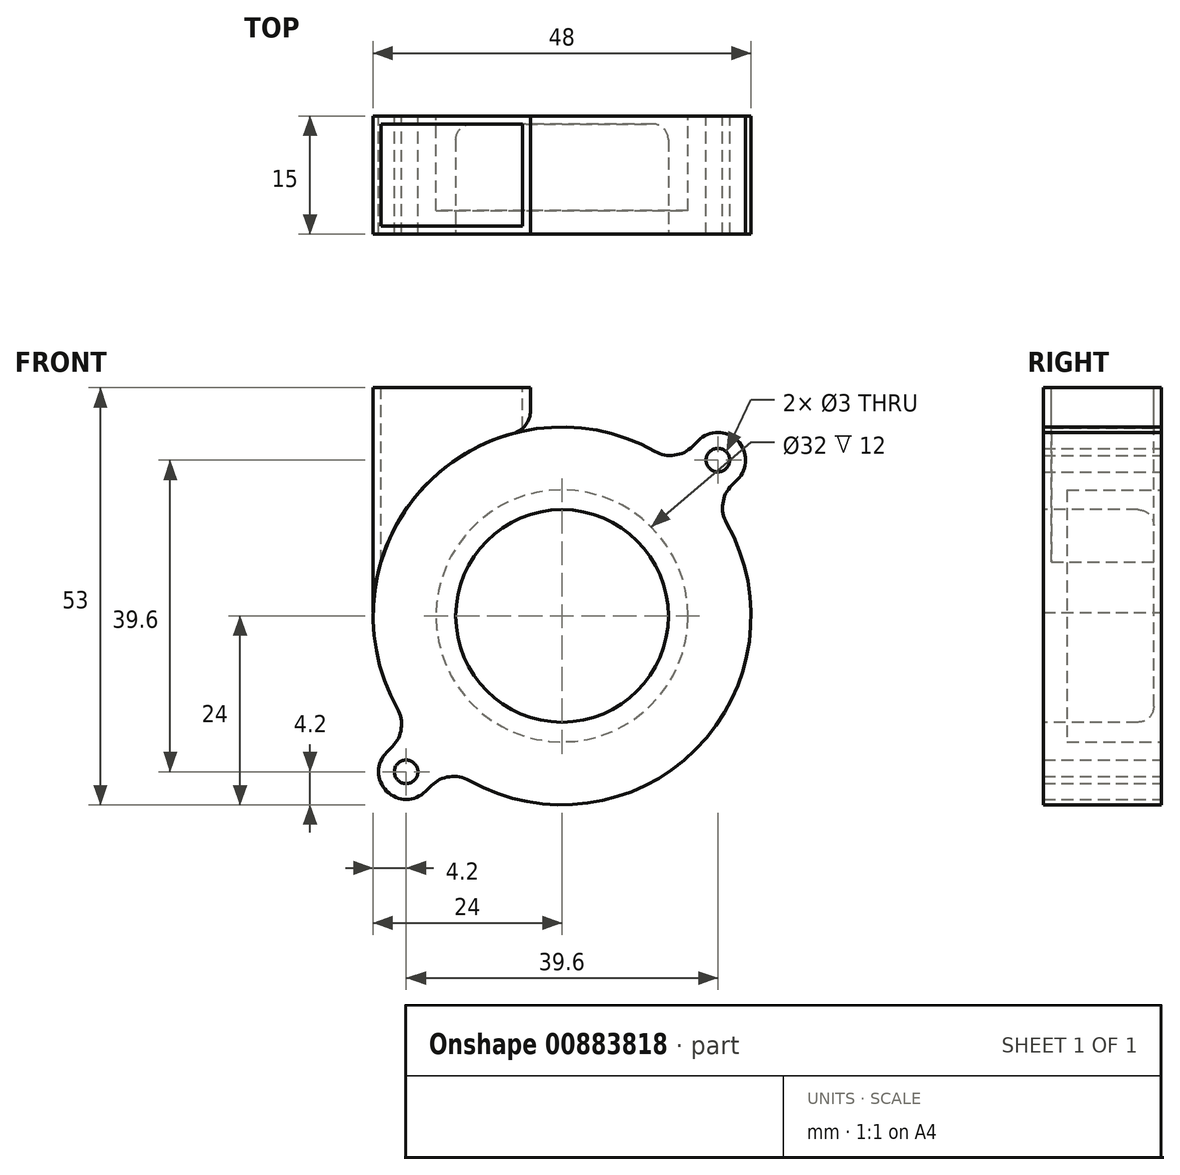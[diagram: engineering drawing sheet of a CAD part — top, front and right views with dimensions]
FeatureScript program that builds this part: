
annotation { "Feature Type Name" : "Feature", "Feature Type Description" : "" }
export const myFeature = defineFeature(function(context is Context, id is Id, definition is map)
    precondition{}
    {
        {
            var Q0;
            Q0=qCreatedBy(makeId("Front.planeOp"),FACE);
            var sketch = newSketch(context, id + "F0", { "sketchPlane" : qUnion([Q0])});
            skArc(sketch, "E0", {"start": v(-11.8, -20.9) * mm, "mid": v(16.97, -16.97) * mm, "end": v(20.9, 11.8) * mm});
            skLineSegment(sketch, "E1", {"start": v(-38.26, -38.26) * mm, "end": v(35.98, 35.98) * mm, "construction": true});
            skCircle(sketch, "E2", {"center": v(-19.8, -19.8) * mm, "radius": 1.5 * mm});
            skCircle(sketch, "E3", {"center": v(19.8, 19.8) * mm, "radius": 1.5 * mm});
            skArc(sketch, "E4", {"start": v(-22.27, -17.32) * mm, "mid": v(-22.27, -22.27) * mm, "end": v(-17.32, -22.27) * mm});
            skArc(sketch, "E5", {"start": v(22.27, 17.32) * mm, "mid": v(22.27, 22.27) * mm, "end": v(17.32, 22.27) * mm});
            skLineSegment(sketch, "E6", {"start": v(-17.32, -22.27) * mm, "end": v(-16.6, -21.55) * mm});
            skLineSegment(sketch, "E7", {"start": v(-22.27, -17.32) * mm, "end": v(-21.55, -16.6) * mm});
            skLineSegment(sketch, "E8.trimOffspring", {"start": v(16.6, 21.55) * mm, "end": v(17.32, 22.27) * mm});
            skLineSegment(sketch, "E9.trimOffspring", {"start": v(21.55, 16.6) * mm, "end": v(22.27, 17.32) * mm});
            skArc(sketch, "E10.trimOffspring", {"start": v(11.8, 20.9) * mm, "mid": v(-16.97, 16.97) * mm, "end": v(-20.9, -11.8) * mm});
            skPoint(sketch, "E11.visualSharp", {"position": v(-14.31, -19.26) * mm});
            skArc(sketch, "E11.filletArc", {"start": v(-11.8, -20.9) * mm, "mid": v(-14.31, -20.42) * mm, "end": v(-16.6, -21.55) * mm});
            skPoint(sketch, "E12.visualSharp", {"position": v(-19.26, -14.31) * mm});
            skArc(sketch, "E12.filletArc", {"start": v(-21.55, -16.6) * mm, "mid": v(-20.42, -14.31) * mm, "end": v(-20.9, -11.8) * mm});
            skPoint(sketch, "E13.visualSharp", {"position": v(19.26, 14.31) * mm});
            skArc(sketch, "E13.filletArc", {"start": v(21.55, 16.6) * mm, "mid": v(20.42, 14.31) * mm, "end": v(20.9, 11.8) * mm});
            skPoint(sketch, "E14.visualSharp", {"position": v(14.31, 19.26) * mm});
            skArc(sketch, "E14.filletArc", {"start": v(11.8, 20.9) * mm, "mid": v(14.31, 20.42) * mm, "end": v(16.6, 21.55) * mm});
            skSolve(sketch);
        }
        {
            var Q0;
            Q0=qSketchRegion(id+"F0",true);
            extrude(context, id + "F1", {"entities" : qUnion([Q0]), "depth" : 15 * mm, "offsetDistance" : 25 * mm, "symmetric" : true});
        }
        {
            var Q0;
            Q0=qCreatedBy(makeId("Top.planeOp"),FACE);
            cPlane(context, id + "F2", {"entities" : qUnion([Q0]), "cplaneType" : CPlaneType.OFFSET, "offset" : 29 * mm, "width" : 150 * mm, "height" : 150 * mm});
        }
        {
            var Q0;
            Q0=qCreatedBy(id+"F2.planeOp",FACE);
            var sketch = newSketch(context, id + "F3", { "sketchPlane" : qUnion([Q0])});
            skLineSegment(sketch, "E15.bottom", {"start": v(-4, 7.5) * mm, "end": v(-24, 7.5) * mm});
            skLineSegment(sketch, "E15.top", {"start": v(-4, -7.5) * mm, "end": v(-24, -7.5) * mm});
            skLineSegment(sketch, "E15.left", {"start": v(-4, 7.5) * mm, "end": v(-4, -7.5) * mm});
            skLineSegment(sketch, "E15.right", {"start": v(-24, 7.5) * mm, "end": v(-24, -7.5) * mm});
            skPoint(sketch, "E15.middle", {"position": v(-14, 0) * mm});
            skSolve(sketch);
        }
        {
            var Q0;
            Q0=qSketchRegion(id+"F3",true);
            var Q1;
            Q1=makeQuery(id+"F1.opExtrude","SWEPT_FACE",FACE,{"disambiguationData":[OSD([sQuery(id+"F0.wireOp",EDGE,"E0")])]});
            extrude(context, id + "F4", {"entities" : qUnion([Q0]), "operationType" : NewBodyOperationType.ADD, "endBound" : BoundingType.UP_TO_SURFACE, "oppositeDirection" : true, "depth" : 25 * mm, "endBoundEntityFace" : qUnion([Q1]), "offsetDistance" : 25 * mm});
        }
        {
            var Q0;
            Q0=makeQuery(id+"F1.opExtrude","CAP_FACE",FACE,{"disambiguationData":[OSD([sQuery(id+"F0.wireOp",EDGE,"E0")])],"isStart":true});
            var sketch = newSketch(context, id + "F5", { "sketchPlane" : qUnion([Q0])});
            skCircle(sketch, "E16", {"center": v(0, 0) * mm, "radius": 16 * mm});
            skSolve(sketch);
        }
        {
            var Q0;
            Q0=qSketchRegion(id+"F5",true);
            extrude(context, id + "F6", {"entities" : qUnion([Q0]), "operationType" : NewBodyOperationType.REMOVE, "oppositeDirection" : true, "depth" : 12 * mm, "offsetDistance" : 25 * mm});
        }
        {
            var Q0;
            Q0=makeQuery(id+"F3.imprint","IMPRINT",FACE,{"disambiguationData":[TD([[makeQuery(id+"F3.imprint","IMPRINT",EDGE,{"derivedFrom":sQuery(id+"F3.wireOp",EDGE,"E15.bottom")}),1.0]])]});
            var sketch = newSketch(context, id + "F7", { "sketchPlane" : qUnion([Q0])});
            skLineSegment(sketch, "E17.0", {"start": v(-23, -6.5) * mm, "end": v(-5, -6.5) * mm});
            skLineSegment(sketch, "E17.1", {"start": v(-23, 6.5) * mm, "end": v(-23, -6.5) * mm});
            skLineSegment(sketch, "E17.2", {"start": v(-5, 6.5) * mm, "end": v(-23, 6.5) * mm});
            skLineSegment(sketch, "E17.3", {"start": v(-5, -6.5) * mm, "end": v(-5, 6.5) * mm});
            skSolve(sketch);
        }
        {
            var Q0;
            Q0=makeQuery(id+"F7.imprint","IMPRINT",FACE,{"disambiguationData":[TD([[makeQuery(id+"F7.imprint","IMPRINT",EDGE,{"derivedFrom":sQuery(id+"F7.wireOp",EDGE,"E17.0")}),1.0]])]});
            var Q1;
            Q1=makeQuery(id+"F1.opExtrude","SWEPT_FACE",FACE,{"disambiguationData":[OSD([sQuery(id+"F0.wireOp",EDGE,"E0")])]});
            extrude(context, id + "F8", {"entities" : qUnion([Q0]), "operationType" : NewBodyOperationType.REMOVE, "endBound" : BoundingType.UP_TO_SURFACE, "oppositeDirection" : true, "depth" : 25 * mm, "endBoundEntityFace" : qUnion([Q1]), "offsetDistance" : 25 * mm});
        }
        {
            var Q0;
            Q0=makeQuery(id+"F4.opExtrude","CAP_EDGE",EDGE,{"disambiguationData":[OSD([sQuery(id+"F3.wireOp",EDGE,"E15.left")])],"isStart":false});
            fillet(context, id + "F9", {"entities" : qUnion([Q0]), "radius" : 3 * mm, "tangentPropagation" : true, "allowEdgeOverflow" : false});
        }
        {
            var Q0;
            Q0=makeQuery(id+"F4.boolean.opBoolean","MERGE",FACE,{"derivedFrom":[makeQuery(id+"F1.opExtrude","CAP_FACE",FACE,{"disambiguationData":[OSD([sQuery(id+"F0.wireOp",EDGE,"E0"),sQuery(id+"F0.wireOp",EDGE,"E2"),sQuery(id+"F0.wireOp",EDGE,"E3"),sQuery(id+"F0.wireOp",EDGE,"E4"),sQuery(id+"F0.wireOp",EDGE,"E5"),sQuery(id+"F0.wireOp",EDGE,"E6"),sQuery(id+"F0.wireOp",EDGE,"E7"),sQuery(id+"F0.wireOp",EDGE,"E8.trimOffspring"),sQuery(id+"F0.wireOp",EDGE,"E9.trimOffspring"),sQuery(id+"F0.wireOp",EDGE,"E10.trimOffspring"),sQuery(id+"F0.wireOp",EDGE,"E11.filletArc"),sQuery(id+"F0.wireOp",EDGE,"E12.filletArc"),sQuery(id+"F0.wireOp",EDGE,"E13.filletArc"),sQuery(id+"F0.wireOp",EDGE,"E14.filletArc")])],"isStart":false}),makeQuery(id+"F4.opExtrude","SWEPT_FACE",FACE,{"disambiguationData":[OSD([sQuery(id+"F3.wireOp",EDGE,"E15.top")])]})]});
            var sketch = newSketch(context, id + "F10", { "sketchPlane" : qUnion([Q0])});
            skCircle(sketch, "E18", {"center": v(0, 0) * mm, "radius": 13.5 * mm});
            skSolve(sketch);
        }
        {
            var Q0;
            Q0=qSketchRegion(id+"F10",true);
            var Q1;
            Q1=qConstructionFilter(qBodyType(qCreatedBy(id+"F10",EDGE),BodyType.WIRE),ConstructionObject.NO);
            extrude(context, id + "F11", {"entities" : qUnion([Q0]), "surfaceEntities" : qUnion([Q1]), "oppositeDirection" : true, "depth" : 14 * mm, "offsetDistance" : 25 * mm});
        }
        {
            var Q0;
            Q0=makeQuery(id+"F11.opExtrude","CAP_EDGE",EDGE,{"disambiguationData":[OSD([sQuery(id+"F10.wireOp",EDGE,"E18")])],"isStart":false});
            fillet(context, id + "F12", {"entities" : qUnion([Q0]), "radius" : 2 * mm, "tangentPropagation" : true, "allowEdgeOverflow" : false});
        }
    });
